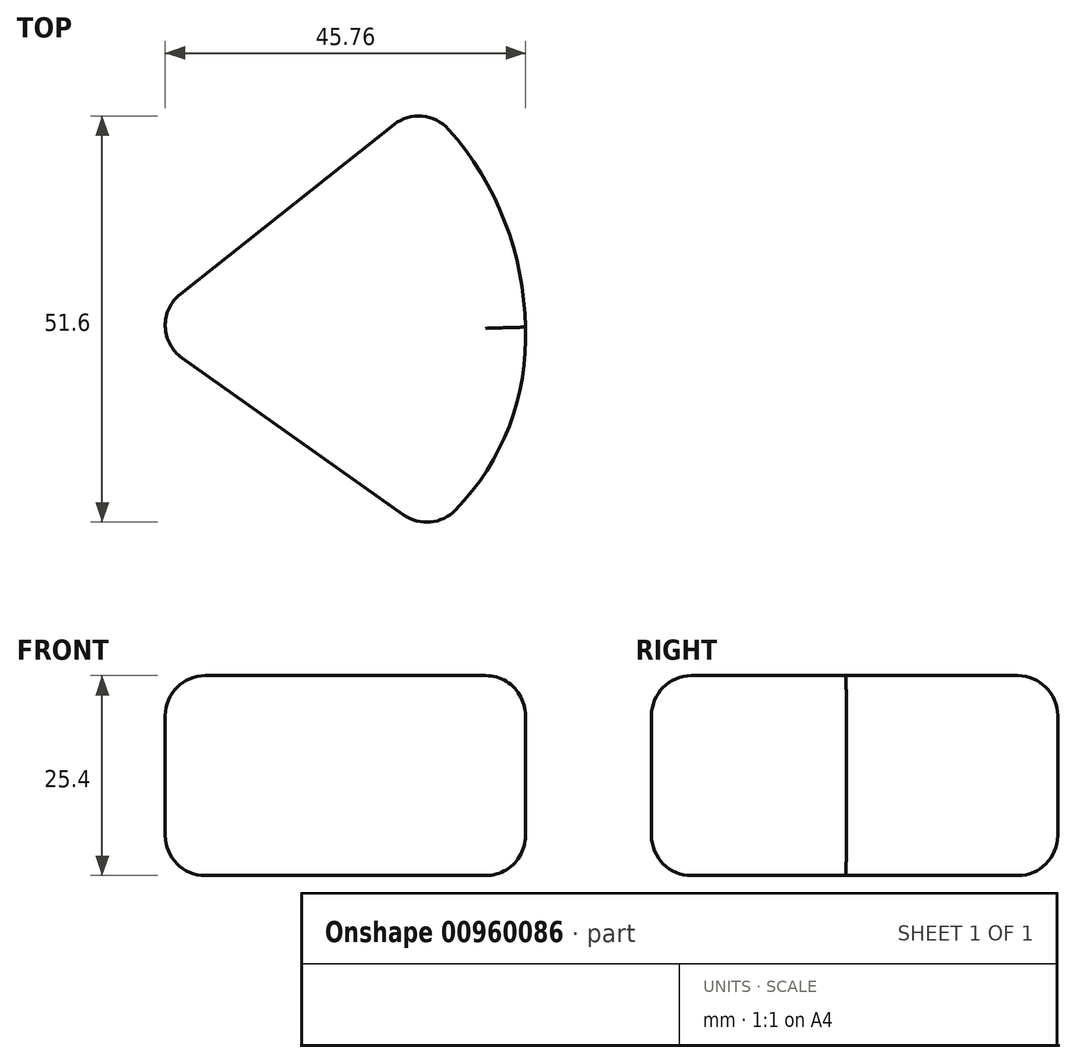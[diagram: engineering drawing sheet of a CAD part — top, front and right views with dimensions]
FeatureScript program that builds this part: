
annotation { "Feature Type Name" : "Feature", "Feature Type Description" : "" }
export const myFeature = defineFeature(function(context is Context, id is Id, definition is map)
    precondition{}
    {
        {
            var Q0;
            Q0=qCreatedBy(makeId("Top.planeOp"),FACE);
            var sketch = newSketch(context, id + "F0", { "sketchPlane" : qUnion([Q0])});
            skArc(sketch, "E0", {"start": v(49.12, 0) * mm, "mid": v(45.57, 15.66) * mm, "end": v(35.95, 28.52) * mm});
            skArc(sketch, "E1", {"start": v(36.97, -26.17) * mm, "mid": v(46.23, -14.56) * mm, "end": v(49.12, 0) * mm});
            skLineSegment(sketch, "E2", {"start": v(0, 0) * mm, "end": v(35.95, 28.52) * mm});
            skLineSegment(sketch, "E3", {"start": v(0, 0) * mm, "end": v(36.97, -26.17) * mm});
            skSolve(sketch);
        }
        {
            var Q0;
            Q0=makeQuery(id+"F0.imprint","IMPRINT",FACE,{"disambiguationData":[TD([[makeQuery(id+"F0.imprint","IMPRINT",EDGE,{"derivedFrom":sQuery(id+"F0.wireOp",EDGE,"E0")}),1.0]])]});
            extrude(context, id + "F1", {"entities" : qUnion([Q0]), "depth" : 25.4 * mm, "offsetDistance" : 25.4 * mm});
        }
        {
            var Q0;
            Q0=makeQuery(id+"F1.opExtrude","SWEPT_EDGE",EDGE,{"disambiguationData":[OSD([sQuery(id+"F0.wireOp",EDGE,"E2"),sQuery(id+"F0.wireOp",EDGE,"E3")])]});
            var Q1;
            Q1=makeQuery(id+"F1.opExtrude","SWEPT_EDGE",EDGE,{"disambiguationData":[OSD([sQuery(id+"F0.wireOp",EDGE,"E1"),sQuery(id+"F0.wireOp",EDGE,"E3")])]});
            var Q2;
            Q2=makeQuery(id+"F1.opExtrude","SWEPT_EDGE",EDGE,{"disambiguationData":[OSD([sQuery(id+"F0.wireOp",EDGE,"E0"),sQuery(id+"F0.wireOp",EDGE,"E2")])]});
            fillet(context, id + "F2", {"entities" : qUnion([Q0, Q1, Q2]), "radius" : 5.08 * mm, "tangentPropagation" : true, "allowEdgeOverflow" : false});
        }
        {
            var Q0;
            Q0=makeQuery(id+"F1.opExtrude","CAP_FACE",FACE,{"disambiguationData":[OSD([sQuery(id+"F0.wireOp",EDGE,"E0"),sQuery(id+"F0.wireOp",EDGE,"E1"),sQuery(id+"F0.wireOp",EDGE,"E2"),sQuery(id+"F0.wireOp",EDGE,"E3")])],"isStart":false});
            var Q1;
            Q1=makeQuery(id+"F1.opExtrude","CAP_FACE",FACE,{"disambiguationData":[OSD([sQuery(id+"F0.wireOp",EDGE,"E0"),sQuery(id+"F0.wireOp",EDGE,"E1"),sQuery(id+"F0.wireOp",EDGE,"E2"),sQuery(id+"F0.wireOp",EDGE,"E3")])],"isStart":true});
            fillet(context, id + "F3", {"entities" : qUnion([Q0, Q1]), "radius" : 5.08 * mm, "tangentPropagation" : true, "allowEdgeOverflow" : false});
        }
    });
